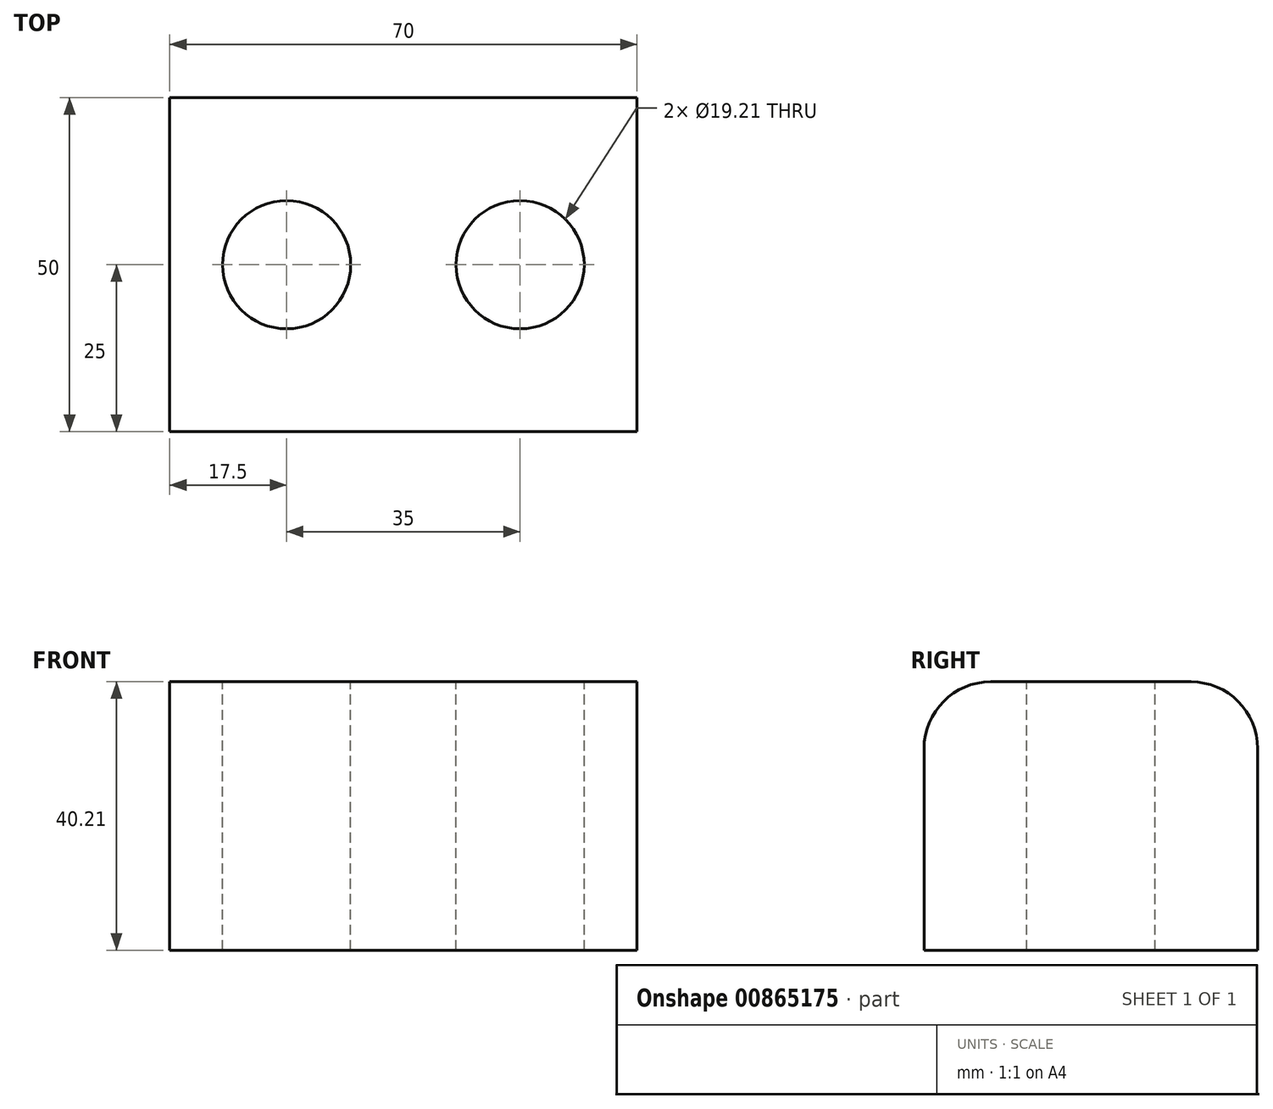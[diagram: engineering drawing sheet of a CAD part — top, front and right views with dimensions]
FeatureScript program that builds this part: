
annotation { "Feature Type Name" : "Feature", "Feature Type Description" : "" }
export const myFeature = defineFeature(function(context is Context, id is Id, definition is map)
    precondition{}
    {
        {
            var Q0;
            Q0=qCreatedBy(makeId("Top.planeOp"),FACE);
            var sketch = newSketch(context, id + "F0", { "sketchPlane" : qUnion([Q0])});
            skLineSegment(sketch, "E0.bottom", {"start": v(35, 50) * mm, "end": v(0, 50) * mm});
            skLineSegment(sketch, "E0.top", {"start": v(35, 0) * mm, "end": v(0, 0) * mm});
            skLineSegment(sketch, "E0.left", {"start": v(35, 50) * mm, "end": v(35, 0) * mm});
            skLineSegment(sketch, "E0.right", {"start": v(0, 50) * mm, "end": v(0, 0) * mm});
            skSolve(sketch);
        }
        {
            var Q0;
            Q0=makeQuery(id+"F0.imprint","IMPRINT",FACE,{"disambiguationData":[TD([[makeQuery(id+"F0.imprint","IMPRINT",EDGE,{"derivedFrom":sQuery(id+"F0.wireOp",EDGE,"E0.bottom")}),1.0]])]});
            extrude(context, id + "F1", {"entities" : qUnion([Q0]), "depth" : 40.2 * mm, "offsetDistance" : 25 * mm});
        }
        {
            var Q0;
            Q0=makeQuery(id+"F1.opExtrude","CAP_EDGE",EDGE,{"disambiguationData":[OSD([sQuery(id+"F0.wireOp",EDGE,"E0.top")])],"isStart":false});
            var Q1;
            Q1=makeQuery(id+"F1.opExtrude","CAP_EDGE",EDGE,{"disambiguationData":[OSD([sQuery(id+"F0.wireOp",EDGE,"E0.bottom")])],"isStart":false});
            fillet(context, id + "F2", {"entities" : qUnion([Q0, Q1]), "radius" : 10 * mm, "tangentPropagation" : true, "allowEdgeOverflow" : false});
        }
        {
            var Q0;
            Q0=makeQuery(id+"F1.opExtrude","CAP_FACE",FACE,{"disambiguationData":[OSD([sQuery(id+"F0.wireOp",EDGE,"E0.bottom"),sQuery(id+"F0.wireOp",EDGE,"E0.top"),sQuery(id+"F0.wireOp",EDGE,"E0.left"),sQuery(id+"F0.wireOp",EDGE,"E0.right")])],"isStart":false});
            var sketch = newSketch(context, id + "F3", { "sketchPlane" : qUnion([Q0])});
            skCircle(sketch, "E1", {"center": v(17.5, 25) * mm, "radius": 9.6 * mm});
            skSolve(sketch);
        }
        {
            var Q0;
            Q0=makeQuery(id+"F3.imprint","IMPRINT",FACE,{"disambiguationData":[TD([[makeQuery(id+"F3.imprint","IMPRINT",EDGE,{"derivedFrom":sQuery(id+"F3.wireOp",EDGE,"E1")}),1.0]])]});
            var Q1;
            Q1=sQuery(id+"F3.wireOp",EDGE,"E1");
            extrude(context, id + "F4", {"entities" : qUnion([Q0]), "operationType" : NewBodyOperationType.REMOVE, "surfaceOperationType" : NewSurfaceOperationType.ADD, "surfaceEntities" : qUnion([Q1]), "oppositeDirection" : true, "depth" : 72.16 * mm, "offsetDistance" : 25 * mm});
        }
        {
            var Q0;
            Q0=makeQuery(id+"F1.opExtrude","SWEPT_BODY",BODY,{"disambiguationData":[OSD([sQuery(id+"F0.wireOp",EDGE,"E0.bottom"),sQuery(id+"F0.wireOp",EDGE,"E0.top"),sQuery(id+"F0.wireOp",EDGE,"E0.left"),sQuery(id+"F0.wireOp",EDGE,"E0.right")])]});
            var Q1;
            Q1=makeQuery(id+"F1.opExtrude","SWEPT_FACE",FACE,{"disambiguationData":[OSD([sQuery(id+"F0.wireOp",EDGE,"E0.left")])]});
            mirror(context, id + "F5", {"operationType" : NewBodyOperationType.ADD, "entities" : qUnion([Q0]), "mirrorPlane" : qUnion([Q1])});
        }
    });
